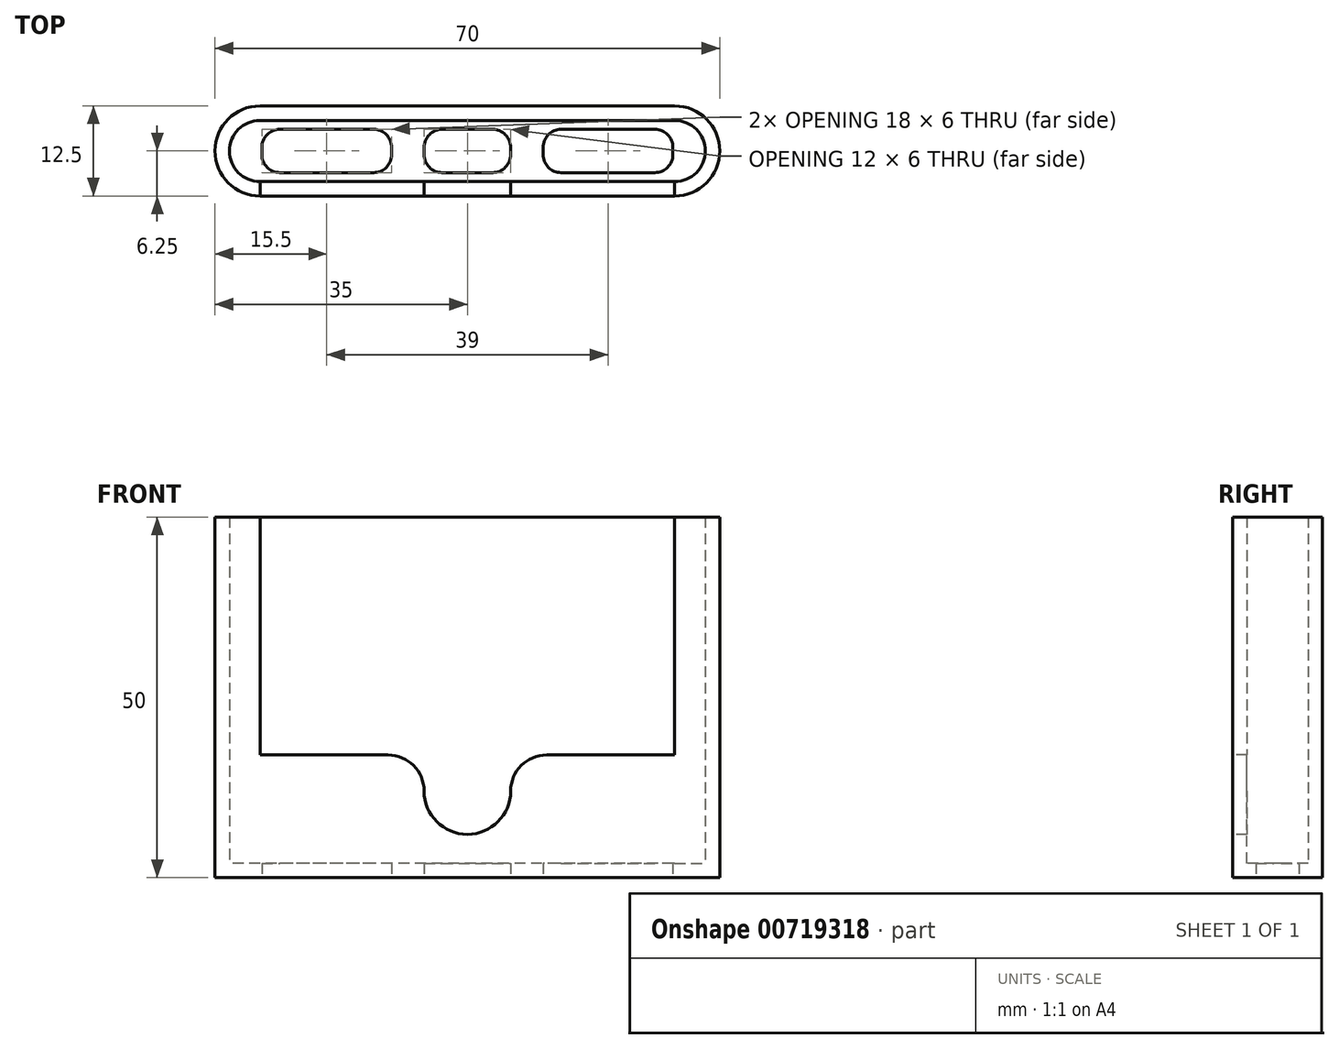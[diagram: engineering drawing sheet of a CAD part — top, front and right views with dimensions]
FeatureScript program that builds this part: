
annotation { "Feature Type Name" : "Feature", "Feature Type Description" : "" }
export const myFeature = defineFeature(function(context is Context, id is Id, definition is map)
    precondition{}
    {
        {
            var Q0;
            Q0=qCreatedBy(makeId("Top.planeOp"),FACE);
            var sketch = newSketch(context, id + "F0", { "sketchPlane" : qUnion([Q0])});
            skLineSegment(sketch, "E0.bottom", {"start": v(28.75, 6.25) * mm, "end": v(-28.75, 6.25) * mm});
            skLineSegment(sketch, "E0.top", {"start": v(28.75, -6.25) * mm, "end": v(-28.75, -6.25) * mm});
            skLineSegment(sketch, "E0.left", {"start": v(35, 0) * mm, "end": v(35, 0) * mm});
            skLineSegment(sketch, "E0.right", {"start": v(-35, 0) * mm, "end": v(-35, 0) * mm});
            skPoint(sketch, "E0.middle", {"position": v(0, 0) * mm});
            skLineSegment(sketch, "E1.bottom", {"start": v(-3.5, -3) * mm, "end": v(3.5, -3) * mm});
            skLineSegment(sketch, "E1.top", {"start": v(-3.5, 3) * mm, "end": v(3.5, 3) * mm});
            skLineSegment(sketch, "E1.left", {"start": v(-6, -0.5) * mm, "end": v(-6, 0.5) * mm});
            skLineSegment(sketch, "E1.right", {"start": v(6, -0.5) * mm, "end": v(6, 0.5) * mm});
            skLineSegment(sketch, "E2", {"start": v(0, -37.66) * mm, "end": v(0, 28.64) * mm, "construction": true});
            skLineSegment(sketch, "E3.bottom", {"start": v(13, 3) * mm, "end": v(26, 3) * mm});
            skLineSegment(sketch, "E3.top", {"start": v(13, -3) * mm, "end": v(26, -3) * mm});
            skLineSegment(sketch, "E3.left", {"start": v(10.5, 0.5) * mm, "end": v(10.5, -0.5) * mm});
            skLineSegment(sketch, "E3.right", {"start": v(28.5, 0.5) * mm, "end": v(28.5, -0.5) * mm});
            skPoint(sketch, "E4.visualSharp", {"position": v(-6, -3) * mm});
            skArc(sketch, "E4.filletArc", {"start": v(-6, -0.5) * mm, "mid": v(-5.27, -2.27) * mm, "end": v(-3.5, -3) * mm});
            skPoint(sketch, "E5.visualSharp", {"position": v(6, 3) * mm});
            skArc(sketch, "E5.filletArc", {"start": v(6, 0.5) * mm, "mid": v(5.27, 2.27) * mm, "end": v(3.5, 3) * mm});
            skPoint(sketch, "E6.visualSharp", {"position": v(6, -3) * mm});
            skArc(sketch, "E6.filletArc", {"start": v(3.5, -3) * mm, "mid": v(5.27, -2.27) * mm, "end": v(6, -0.5) * mm});
            skPoint(sketch, "E7.visualSharp", {"position": v(-6, 3) * mm});
            skArc(sketch, "E7.filletArc", {"start": v(-3.5, 3) * mm, "mid": v(-5.27, 2.27) * mm, "end": v(-6, 0.5) * mm});
            skLineSegment(sketch, "E8.MirrorCS", {"start": v(-13, 3) * mm, "end": v(-26, 3) * mm});
            skLineSegment(sketch, "E9.MirrorCS", {"start": v(-10.5, 0.5) * mm, "end": v(-10.5, -0.5) * mm});
            skLineSegment(sketch, "E10.MirrorCS", {"start": v(-13, -3) * mm, "end": v(-26, -3) * mm});
            skLineSegment(sketch, "E11.MirrorCS", {"start": v(-28.5, 0.5) * mm, "end": v(-28.5, -0.5) * mm});
            skPoint(sketch, "E12.visualSharp", {"position": v(10.5, -3) * mm});
            skArc(sketch, "E12.filletArc", {"start": v(10.5, -0.5) * mm, "mid": v(11.23, -2.27) * mm, "end": v(13, -3) * mm});
            skPoint(sketch, "E13.visualSharp", {"position": v(10.5, 3) * mm});
            skArc(sketch, "E13.filletArc", {"start": v(13, 3) * mm, "mid": v(11.23, 2.27) * mm, "end": v(10.5, 0.5) * mm});
            skPoint(sketch, "E14.visualSharp", {"position": v(28.5, 3) * mm});
            skArc(sketch, "E14.filletArc", {"start": v(28.5, 0.5) * mm, "mid": v(27.77, 2.27) * mm, "end": v(26, 3) * mm});
            skPoint(sketch, "E15.visualSharp", {"position": v(28.5, -3) * mm});
            skArc(sketch, "E15.filletArc", {"start": v(26, -3) * mm, "mid": v(27.77, -2.27) * mm, "end": v(28.5, -0.5) * mm});
            skPoint(sketch, "E16.visualSharp", {"position": v(-10.5, -3) * mm});
            skArc(sketch, "E16.filletArc", {"start": v(-13, -3) * mm, "mid": v(-11.23, -2.27) * mm, "end": v(-10.5, -0.5) * mm});
            skPoint(sketch, "E17.visualSharp", {"position": v(-10.5, 3) * mm});
            skArc(sketch, "E17.filletArc", {"start": v(-10.5, 0.5) * mm, "mid": v(-11.23, 2.27) * mm, "end": v(-13, 3) * mm});
            skPoint(sketch, "E18.visualSharp", {"position": v(-28.5, 3) * mm});
            skArc(sketch, "E18.filletArc", {"start": v(-26, 3) * mm, "mid": v(-27.77, 2.27) * mm, "end": v(-28.5, 0.5) * mm});
            skPoint(sketch, "E19.visualSharp", {"position": v(-28.5, -3) * mm});
            skArc(sketch, "E19.filletArc", {"start": v(-28.5, -0.5) * mm, "mid": v(-27.77, -2.27) * mm, "end": v(-26, -3) * mm});
            skPoint(sketch, "E20.visualSharp", {"position": v(-35, -6.25) * mm});
            skArc(sketch, "E20.filletArc", {"start": v(-35, 0) * mm, "mid": v(-33.17, -4.42) * mm, "end": v(-28.75, -6.25) * mm});
            skPoint(sketch, "E21.visualSharp", {"position": v(-35, 6.25) * mm});
            skArc(sketch, "E21.filletArc", {"start": v(-28.75, 6.25) * mm, "mid": v(-33.17, 4.42) * mm, "end": v(-35, 0) * mm});
            skPoint(sketch, "E22.visualSharp", {"position": v(35, 6.25) * mm});
            skArc(sketch, "E22.filletArc", {"start": v(35, 0) * mm, "mid": v(33.17, 4.42) * mm, "end": v(28.75, 6.25) * mm});
            skPoint(sketch, "E23.visualSharp", {"position": v(35, -6.25) * mm});
            skArc(sketch, "E23.filletArc", {"start": v(28.75, -6.25) * mm, "mid": v(33.17, -4.42) * mm, "end": v(35, 0) * mm});
            skArc(sketch, "E24.0", {"start": v(28.75, -4.25) * mm, "mid": v(31.76, -3) * mm, "end": v(33, 0) * mm});
            skArc(sketch, "E24.1", {"start": v(-33, 0) * mm, "mid": v(-31.76, -3) * mm, "end": v(-28.75, -4.25) * mm});
            skArc(sketch, "E24.2", {"start": v(-28.75, 4.25) * mm, "mid": v(-31.76, 3) * mm, "end": v(-33, 0) * mm});
            skLineSegment(sketch, "E24.3", {"start": v(28.75, -4.25) * mm, "end": v(-28.75, -4.25) * mm});
            skLineSegment(sketch, "E24.4", {"start": v(28.75, 4.25) * mm, "end": v(-28.75, 4.25) * mm});
            skArc(sketch, "E24.5", {"start": v(33, 0) * mm, "mid": v(31.76, 3) * mm, "end": v(28.75, 4.25) * mm});
            skLineSegment(sketch, "E25", {"start": v(-28.75, -4.25) * mm, "end": v(-28.75, -6.25) * mm});
            skLineSegment(sketch, "E26", {"start": v(28.75, -6.25) * mm, "end": v(28.75, -4.25) * mm});
            skPoint(sketch, "E27.startSnap0", {"position": v(19.5, 0) * mm});
            skSolve(sketch);
        }
        {
            var Q0;
            Q0=sQuery(id+"F0.wireOp",EDGE,"E0.top");
            cPlane(context, id + "F1", {"entities" : qUnion([Q0]), "cplaneType" : CPlaneType.LINE_ANGLE, "offset" : 25 * mm, "angle" : 0 * degree, "width" : 150 * mm, "height" : 150 * mm});
        }
        {
            var Q0;
            Q0=qCreatedBy(id+"F1.planeOp",FACE);
            var sketch = newSketch(context, id + "F2", { "sketchPlane" : qUnion([Q0])});
            skLineSegment(sketch, "E28.bottom", {"start": v(-28.75, 0) * mm, "end": v(28.75, 0) * mm});
            skLineSegment(sketch, "E28.top", {"start": v(-28.75, 17) * mm, "end": v(-11, 17) * mm});
            skLineSegment(sketch, "E28.left", {"start": v(-28.75, 0) * mm, "end": v(-28.75, 17) * mm});
            skLineSegment(sketch, "E28.right", {"start": v(28.75, 0) * mm, "end": v(28.75, 17) * mm});
            skLineSegment(sketch, "E29.trimOffspring", {"start": v(11, 17) * mm, "end": v(28.75, 17) * mm});
            skLineSegment(sketch, "E30.top", {"start": v(0, 6) * mm, "end": v(0, 6) * mm});
            skLineSegment(sketch, "E30.left", {"start": v(-6, 12) * mm, "end": v(-6, 12) * mm});
            skLineSegment(sketch, "E30.right", {"start": v(6, 12) * mm, "end": v(6, 12) * mm});
            skPoint(sketch, "E30.middle", {"position": v(0, 14.54) * mm});
            skPoint(sketch, "E31.orphan", {"position": v(6, 23.08) * mm});
            skPoint(sketch, "E32.orphan", {"position": v(-6, 23.08) * mm});
            skPoint(sketch, "E33.visualSharp", {"position": v(-6, 6) * mm});
            skArc(sketch, "E33.filletArc", {"start": v(-6, 12) * mm, "mid": v(-4.24, 7.76) * mm, "end": v(0, 6) * mm});
            skPoint(sketch, "E34.visualSharp", {"position": v(6, 6) * mm});
            skArc(sketch, "E34.filletArc", {"start": v(0, 6) * mm, "mid": v(4.24, 7.76) * mm, "end": v(6, 12) * mm});
            skPoint(sketch, "E35.visualSharp", {"position": v(6, 17) * mm});
            skArc(sketch, "E35.filletArc", {"start": v(11, 17) * mm, "mid": v(7.46, 15.54) * mm, "end": v(6, 12) * mm});
            skPoint(sketch, "E36.visualSharp", {"position": v(-6, 17) * mm});
            skArc(sketch, "E36.filletArc", {"start": v(-6, 12) * mm, "mid": v(-7.46, 15.54) * mm, "end": v(-11, 17) * mm});
            skSolve(sketch);
        }
        {
            var Q0;
            Q0=makeQuery(id+"F0.imprint","IMPRINT",FACE,{"disambiguationData":[TD([[makeQuery(id+"F0.imprint","IMPRINT",EDGE,{"derivedFrom":sQuery(id+"F0.wireOp",EDGE,"E0.bottom")}),1.0]])]});
            extrude(context, id + "F3", {"entities" : qUnion([Q0]), "depth" : 50 * mm, "offsetDistance" : 25 * mm});
        }
        {
            var Q0;
            Q0=makeQuery(id+"F0.imprint","IMPRINT",FACE,{"disambiguationData":[TD([[makeQuery(id+"F0.imprint","IMPRINT",EDGE,{"derivedFrom":sQuery(id+"F0.wireOp",EDGE,"E1.bottom")}),-1.0]])]});
            extrude(context, id + "F4", {"entities" : qUnion([Q0]), "operationType" : NewBodyOperationType.ADD, "depth" : 2 * mm, "offsetDistance" : 25 * mm});
        }
        {
            var Q0;
            Q0=qSketchRegion(id+"F2",true);
            extrude(context, id + "F5", {"entities" : qUnion([Q0]), "operationType" : NewBodyOperationType.ADD, "oppositeDirection" : true, "depth" : 2 * mm, "offsetDistance" : 25 * mm});
        }
    });
